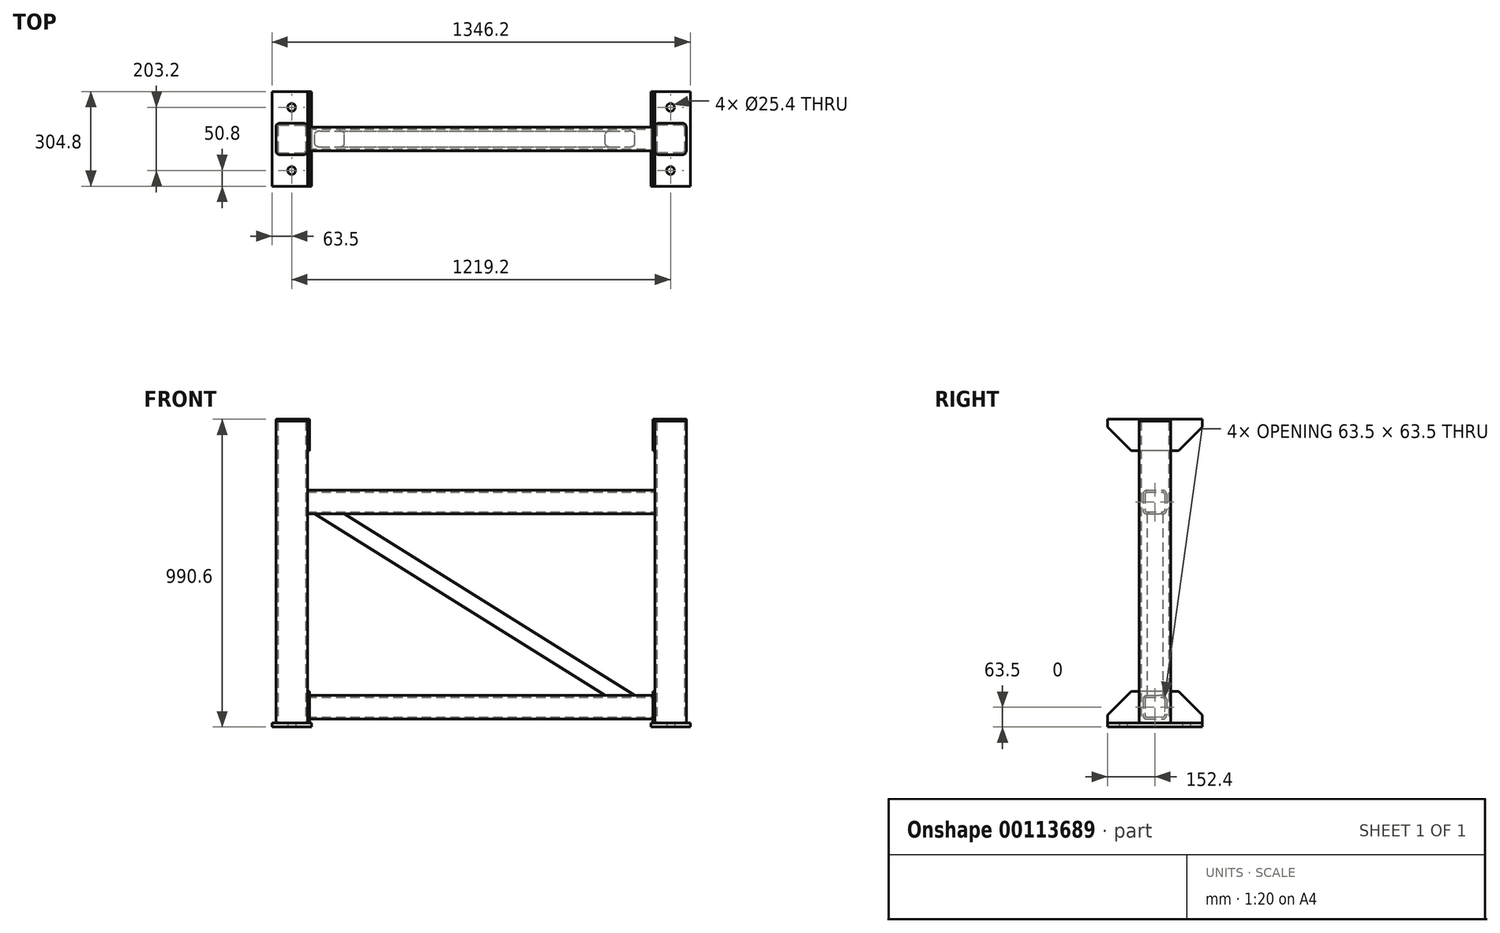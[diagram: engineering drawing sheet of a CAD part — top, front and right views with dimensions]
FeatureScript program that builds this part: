
annotation { "Feature Type Name" : "Feature", "Feature Type Description" : "" }
export const myFeature = defineFeature(function(context is Context, id is Id, definition is map)
    precondition{}
    {
        {
            var Q0;
            Q0=qCreatedBy(makeId("Top.planeOp"),FACE);
            var sketch = newSketch(context, id + "F0", { "sketchPlane" : qUnion([Q0])});
            skLineSegment(sketch, "E0", {"start": v(-609.6, 0) * mm, "end": v(157.5, 0) * mm, "construction": true});
            skLineSegment(sketch, "E1", {"start": v(0, 108.34) * mm, "end": v(0, -86.64) * mm, "construction": true});
            skLineSegment(sketch, "E2.0", {"start": v(-609.6, 108.34) * mm, "end": v(-609.6, -86.64) * mm, "construction": true});
            skPoint(sketch, "E3.orphan", {"position": v(-161.92, 0) * mm});
            skLineSegment(sketch, "E4.bottom", {"start": v(-673.1, 152.4) * mm, "end": v(-546.1, 152.4) * mm});
            skLineSegment(sketch, "E4.top", {"start": v(-673.1, -152.4) * mm, "end": v(-546.1, -152.4) * mm});
            skLineSegment(sketch, "E4.left", {"start": v(-673.1, 152.4) * mm, "end": v(-673.1, -152.4) * mm});
            skLineSegment(sketch, "E4.right", {"start": v(-546.1, 152.4) * mm, "end": v(-546.1, -152.4) * mm});
            skPoint(sketch, "E4.middle", {"position": v(-609.6, 0) * mm});
            skLineSegment(sketch, "E5.0", {"start": v(-609.6, 101.6) * mm, "end": v(157.5, 101.6) * mm, "construction": true});
            skCircle(sketch, "E6", {"center": v(-609.6, 101.6) * mm, "radius": 12.7 * mm});
            skCircle(sketch, "E7.MirrorC", {"center": v(-609.6, -101.6) * mm, "radius": 12.7 * mm});
            skSolve(sketch);
        }
        {
            var Q0;
            Q0 = qSketchRegion(id + "F0", true);
            extrude(context, id + "F1", {"entities" : qUnion([Q0]), "depth" : 12.7 * mm});
        }
        {
            var Q0;
            Q0=makeQuery(id+"F1.opExtrude","CAP_FACE",FACE,{"disambiguationData":[OSD([sQuery(id+"F0.wireOp",EDGE,"E4.bottom"),sQuery(id+"F0.wireOp",EDGE,"E4.top"),sQuery(id+"F0.wireOp",EDGE,"E4.left"),sQuery(id+"F0.wireOp",EDGE,"E4.right"),sQuery(id+"F0.wireOp",EDGE,"E6"),sQuery(id+"F0.wireOp",EDGE,"E7.MirrorC")])],"isStart":false});
            var sketch = newSketch(context, id + "F2", { "sketchPlane" : qUnion([Q0])});
            skLineSegment(sketch, "E8", {"start": v(-673.1, 0) * mm, "end": v(-546.1, 0) * mm, "construction": true});
            skLineSegment(sketch, "E9.bottom", {"start": v(-647.7, 50.8) * mm, "end": v(-571.5, 50.8) * mm});
            skLineSegment(sketch, "E9.top", {"start": v(-647.7, -50.8) * mm, "end": v(-571.5, -50.8) * mm});
            skLineSegment(sketch, "E9.left", {"start": v(-660.4, 38.1) * mm, "end": v(-660.4, -38.1) * mm});
            skLineSegment(sketch, "E9.right", {"start": v(-558.8, 38.1) * mm, "end": v(-558.8, -38.1) * mm});
            skPoint(sketch, "E9.middle", {"position": v(-609.6, 0) * mm});
            skPoint(sketch, "E10.visualSharp", {"position": v(-660.4, 50.8) * mm});
            skArc(sketch, "E10.filletArc", {"start": v(-647.7, 50.8) * mm, "mid": v(-656.68, 47.08) * mm, "end": v(-660.4, 38.1) * mm});
            skPoint(sketch, "E11.visualSharp", {"position": v(-558.8, 50.8) * mm});
            skArc(sketch, "E11.filletArc", {"start": v(-558.8, 38.1) * mm, "mid": v(-562.52, 47.08) * mm, "end": v(-571.5, 50.8) * mm});
            skPoint(sketch, "E12.visualSharp", {"position": v(-558.8, -50.8) * mm});
            skArc(sketch, "E12.filletArc", {"start": v(-571.5, -50.8) * mm, "mid": v(-562.52, -47.08) * mm, "end": v(-558.8, -38.1) * mm});
            skPoint(sketch, "E13.visualSharp", {"position": v(-660.4, -50.8) * mm});
            skArc(sketch, "E13.filletArc", {"start": v(-660.4, -38.1) * mm, "mid": v(-656.68, -47.08) * mm, "end": v(-647.7, -50.8) * mm});
            skArc(sketch, "E14.0", {"start": v(-647.7, 44.45) * mm, "mid": v(-652.2, 42.6) * mm, "end": v(-654.05, 38.1) * mm});
            skLineSegment(sketch, "E14.1", {"start": v(-654.05, 38.1) * mm, "end": v(-654.05, -38.1) * mm});
            skLineSegment(sketch, "E14.2", {"start": v(-647.7, 44.45) * mm, "end": v(-571.5, 44.45) * mm});
            skArc(sketch, "E14.3", {"start": v(-654.05, -38.1) * mm, "mid": v(-652.2, -42.6) * mm, "end": v(-647.7, -44.45) * mm});
            skArc(sketch, "E14.4", {"start": v(-565.15, 38.1) * mm, "mid": v(-567, 42.6) * mm, "end": v(-571.5, 44.45) * mm});
            skLineSegment(sketch, "E14.5", {"start": v(-565.15, 38.1) * mm, "end": v(-565.15, -38.1) * mm});
            skArc(sketch, "E14.6", {"start": v(-571.5, -44.45) * mm, "mid": v(-567, -42.6) * mm, "end": v(-565.15, -38.1) * mm});
            skLineSegment(sketch, "E14.7", {"start": v(-647.7, -44.45) * mm, "end": v(-571.5, -44.45) * mm});
            skSolve(sketch);
        }
        {
            var Q0;
            Q0 = qSketchRegion(id + "F2", true);
            extrude(context, id + "F3", {"entities" : qUnion([Q0]), "operationType" : NewBodyOperationType.ADD, "depth" : 971.55 * mm});
        }
        {
            var Q0;
            Q0=makeQuery(id+"F3.opExtrude","CAP_FACE",FACE,{"disambiguationData":[OSD([sQuery(id+"F2.wireOp",EDGE,"E9.bottom"),sQuery(id+"F2.wireOp",EDGE,"E9.top"),sQuery(id+"F2.wireOp",EDGE,"E9.left"),sQuery(id+"F2.wireOp",EDGE,"E9.right"),sQuery(id+"F2.wireOp",EDGE,"E10.filletArc"),sQuery(id+"F2.wireOp",EDGE,"E11.filletArc"),sQuery(id+"F2.wireOp",EDGE,"E12.filletArc"),sQuery(id+"F2.wireOp",EDGE,"E13.filletArc"),sQuery(id+"F2.wireOp",EDGE,"E14.0"),sQuery(id+"F2.wireOp",EDGE,"E14.1"),sQuery(id+"F2.wireOp",EDGE,"E14.2"),sQuery(id+"F2.wireOp",EDGE,"E14.3"),sQuery(id+"F2.wireOp",EDGE,"E14.4"),sQuery(id+"F2.wireOp",EDGE,"E14.5"),sQuery(id+"F2.wireOp",EDGE,"E14.6"),sQuery(id+"F2.wireOp",EDGE,"E14.7")])],"isStart":false});
            var sketch = newSketch(context, id + "F4", { "sketchPlane" : qUnion([Q0])});
            skLineSegment(sketch, "E15.0", {"start": v(-660.4, 38.1) * mm, "end": v(-660.4, -38.1) * mm});
            skArc(sketch, "E16.0", {"start": v(-647.7, 50.8) * mm, "mid": v(-656.68, 47.08) * mm, "end": v(-660.4, 38.1) * mm});
            skLineSegment(sketch, "E17.0", {"start": v(-647.7, 50.8) * mm, "end": v(-571.5, 50.8) * mm});
            skArc(sketch, "E18.0", {"start": v(-558.8, 38.1) * mm, "mid": v(-562.52, 47.08) * mm, "end": v(-571.5, 50.8) * mm});
            skLineSegment(sketch, "E19.0", {"start": v(-558.8, 38.1) * mm, "end": v(-558.8, -38.1) * mm});
            skArc(sketch, "E20.0", {"start": v(-571.5, -50.8) * mm, "mid": v(-562.52, -47.08) * mm, "end": v(-558.8, -38.1) * mm});
            skLineSegment(sketch, "E21.0", {"start": v(-647.7, -50.8) * mm, "end": v(-571.5, -50.8) * mm});
            skArc(sketch, "E22.0", {"start": v(-660.4, -38.1) * mm, "mid": v(-656.68, -47.08) * mm, "end": v(-647.7, -50.8) * mm});
            skSolve(sketch);
        }
        {
            var Q0;
            Q0 = qSketchRegion(id + "F4", true);
            extrude(context, id + "F5", {"entities" : qUnion([Q0]), "depth" : 6.35 * mm});
        }
        {
            var Q0;
            Q0=makeQuery(id+"F5.boolean.opBoolean","MERGE",FACE,{"derivedFrom":[makeQuery(id+"F3.opExtrude","SWEPT_FACE",FACE,{"disambiguationData":[OSD([sQuery(id+"F2.wireOp",EDGE,"E9.right")])]}),makeQuery(id+"F5.opExtrude","SWEPT_FACE",FACE,{"disambiguationData":[OSD([sQuery(id+"F4.wireOp",EDGE,"E19.0")])]})]});
            var sketch = newSketch(context, id + "F6", { "sketchPlane" : qUnion([Q0])});
            skLineSegment(sketch, "E23.0", {"start": v(152.4, 12.7) * mm, "end": v(-152.4, 12.7) * mm});
            skLineSegment(sketch, "E24.0", {"start": v(76.2, 114.3) * mm, "end": v(-76.2, 114.3) * mm});
            skLineSegment(sketch, "E25", {"start": v(-152.4, 38.1) * mm, "end": v(-152.4, 12.7) * mm});
            skLineSegment(sketch, "E26", {"start": v(152.4, 38.1) * mm, "end": v(152.4, 12.7) * mm});
            skLineSegment(sketch, "E27", {"start": v(-152.4, 38.1) * mm, "end": v(-76.2, 114.3) * mm});
            skLineSegment(sketch, "E28", {"start": v(76.2, 114.3) * mm, "end": v(152.4, 38.1) * mm});
            skSolve(sketch);
        }
        {
            var Q0;
            Q0 = qSketchRegion(id + "F6", true);
            extrude(context, id + "F7", {"entities" : qUnion([Q0]), "depth" : 6.35 * mm});
        }
        {
            var Q0;
            Q0=makeQuery(id+"F7.opExtrude","SWEPT_BODY",BODY,{"disambiguationData":[OSD([sQuery(id+"F6.wireOp",EDGE,"E23.0"),sQuery(id+"F6.wireOp",EDGE,"E24.0"),sQuery(id+"F6.wireOp",EDGE,"E25"),sQuery(id+"F6.wireOp",EDGE,"E26"),sQuery(id+"F6.wireOp",EDGE,"E27"),sQuery(id+"F6.wireOp",EDGE,"E28")])]});
            var Q1;
            Q1=makeQuery(id+"F5.opExtrude","CAP_FACE",FACE,{"disambiguationData":[OSD([sQuery(id+"F4.wireOp",EDGE,"E15.0"),sQuery(id+"F4.wireOp",EDGE,"E16.0"),sQuery(id+"F4.wireOp",EDGE,"E17.0"),sQuery(id+"F4.wireOp",EDGE,"E18.0"),sQuery(id+"F4.wireOp",EDGE,"E19.0"),sQuery(id+"F4.wireOp",EDGE,"E20.0"),sQuery(id+"F4.wireOp",EDGE,"E21.0"),sQuery(id+"F4.wireOp",EDGE,"E22.0")])],"isStart":false});
            mirror(context, id + "F8", {"entities" : qUnion([Q0]), "mirrorPlane" : qUnion([Q1])});
        }
        {
            var Q0;
            Q0=makeQuery(id+"F8.opPattern","COPY",BODY,{"derivedFrom":makeQuery(id+"F7.opExtrude","SWEPT_BODY",BODY,{"disambiguationData":[OSD([sQuery(id+"F6.wireOp",EDGE,"E23.0"),sQuery(id+"F6.wireOp",EDGE,"E24.0"),sQuery(id+"F6.wireOp",EDGE,"E25"),sQuery(id+"F6.wireOp",EDGE,"E26"),sQuery(id+"F6.wireOp",EDGE,"E27"),sQuery(id+"F6.wireOp",EDGE,"E28")])]}),"instanceName":"1"});
            var Q1;
            Q1=makeQuery(id+"F3.opExtrude","SWEPT_EDGE",EDGE,{"disambiguationData":[OSD([sQuery(id+"F2.wireOp",EDGE,"E9.bottom"),sQuery(id+"F2.wireOp",EDGE,"E11.filletArc")])]});
            transform(context, id + "F9", {"entities" : qUnion([Q0]), "transformType" : TransformType.TRANSLATION_ENTITY, "oppositeDirectionEntity" : false, "transformLine" : qUnion([Q1]), "makeCopy" : false});
        }
        {
            var Q0;
            Q0=makeQuery(id+"F8.opPattern","COPY",BODY,{"derivedFrom":makeQuery(id+"F7.opExtrude","SWEPT_BODY",BODY,{"disambiguationData":[OSD([sQuery(id+"F6.wireOp",EDGE,"E23.0"),sQuery(id+"F6.wireOp",EDGE,"E24.0"),sQuery(id+"F6.wireOp",EDGE,"E25"),sQuery(id+"F6.wireOp",EDGE,"E26"),sQuery(id+"F6.wireOp",EDGE,"E27"),sQuery(id+"F6.wireOp",EDGE,"E28")])]}),"instanceName":"1"});
            var Q1;
            Q1=makeQuery(id+"F8.opPattern","COPY",EDGE,{"derivedFrom":makeQuery(id+"F7.opExtrude","CAP_EDGE",EDGE,{"disambiguationData":[OSD([sQuery(id+"F6.wireOp",EDGE,"E26")])],"isStart":false}),"instanceName":"1"});
            transform(context, id + "F10", {"entities" : qUnion([Q0]), "transformType" : TransformType.TRANSLATION_DISTANCE, "transformDirection" : qUnion([Q1]), "distance" : 6.35 * mm, "oppositeDirection" : true, "makeCopy" : false});
        }
        {
            var Q0;
            Q0=makeQuery(id+"F3.opExtrude","SWEPT_FACE",FACE,{"disambiguationData":[OSD([sQuery(id+"F2.wireOp",EDGE,"E9.right")])]});
            var sketch = newSketch(context, id + "F11", { "sketchPlane" : qUnion([Q0])});
            skLineSegment(sketch, "E29.0", {"start": v(152.4, 0) * mm, "end": v(-152.4, 0) * mm, "construction": true});
            skLineSegment(sketch, "E30.0", {"start": v(152.4, 63.5) * mm, "end": v(-152.4, 63.5) * mm, "construction": true});
            skLineSegment(sketch, "E31.bottom", {"start": v(-25.4, 101.6) * mm, "end": v(25.4, 101.6) * mm});
            skLineSegment(sketch, "E31.top", {"start": v(-25.4, 25.4) * mm, "end": v(25.4, 25.4) * mm});
            skLineSegment(sketch, "E31.left", {"start": v(-38.1, 88.9) * mm, "end": v(-38.1, 38.1) * mm});
            skLineSegment(sketch, "E31.right", {"start": v(38.1, 88.9) * mm, "end": v(38.1, 38.1) * mm});
            skPoint(sketch, "E31.middle", {"position": v(0, 63.5) * mm});
            skPoint(sketch, "E32.visualSharp", {"position": v(-38.1, 101.6) * mm});
            skArc(sketch, "E32.filletArc", {"start": v(-25.4, 101.6) * mm, "mid": v(-34.38, 97.88) * mm, "end": v(-38.1, 88.9) * mm});
            skPoint(sketch, "E33.visualSharp", {"position": v(38.1, 101.6) * mm});
            skArc(sketch, "E33.filletArc", {"start": v(38.1, 88.9) * mm, "mid": v(34.38, 97.88) * mm, "end": v(25.4, 101.6) * mm});
            skPoint(sketch, "E34.visualSharp", {"position": v(38.1, 25.4) * mm});
            skArc(sketch, "E34.filletArc", {"start": v(25.4, 25.4) * mm, "mid": v(34.38, 29.12) * mm, "end": v(38.1, 38.1) * mm});
            skPoint(sketch, "E35.visualSharp", {"position": v(-38.1, 25.4) * mm});
            skArc(sketch, "E35.filletArc", {"start": v(-38.1, 38.1) * mm, "mid": v(-34.38, 29.12) * mm, "end": v(-25.4, 25.4) * mm});
            skArc(sketch, "E36.0", {"start": v(-25.4, 95.25) * mm, "mid": v(-29.9, 93.4) * mm, "end": v(-31.75, 88.9) * mm});
            skLineSegment(sketch, "E36.1", {"start": v(-31.75, 88.9) * mm, "end": v(-31.75, 38.1) * mm});
            skLineSegment(sketch, "E36.2", {"start": v(-25.4, 95.25) * mm, "end": v(25.4, 95.25) * mm});
            skArc(sketch, "E36.3", {"start": v(-31.75, 38.1) * mm, "mid": v(-29.9, 33.6) * mm, "end": v(-25.4, 31.75) * mm});
            skArc(sketch, "E36.4", {"start": v(31.75, 88.9) * mm, "mid": v(29.9, 93.4) * mm, "end": v(25.4, 95.25) * mm});
            skLineSegment(sketch, "E36.5", {"start": v(31.75, 88.9) * mm, "end": v(31.75, 38.1) * mm});
            skArc(sketch, "E36.6", {"start": v(25.4, 31.75) * mm, "mid": v(29.9, 33.6) * mm, "end": v(31.75, 38.1) * mm});
            skLineSegment(sketch, "E36.7", {"start": v(-25.4, 31.75) * mm, "end": v(25.4, 31.75) * mm});
            skPoint(sketch, "E37.0.1.0", {"position": v(38.1, 762) * mm});
            skPoint(sketch, "E37.0.1.1", {"position": v(38.1, 685.8) * mm});
            skPoint(sketch, "E37.0.1.2", {"position": v(-38.1, 762) * mm});
            skPoint(sketch, "E37.0.1.3", {"position": v(-38.1, 685.8) * mm});
            skLineSegment(sketch, "E37.0.1.4", {"start": v(31.75, 749.3) * mm, "end": v(31.75, 698.5) * mm});
            skPoint(sketch, "E37.0.1.5", {"position": v(0, 723.9) * mm});
            skLineSegment(sketch, "E37.0.1.6", {"start": v(-38.1, 749.3) * mm, "end": v(-38.1, 698.5) * mm});
            skLineSegment(sketch, "E37.0.1.7", {"start": v(38.1, 749.3) * mm, "end": v(38.1, 698.5) * mm});
            skLineSegment(sketch, "E37.0.1.8", {"start": v(-31.75, 749.3) * mm, "end": v(-31.75, 698.5) * mm});
            skLineSegment(sketch, "E37.0.1.9", {"start": v(-25.4, 685.8) * mm, "end": v(25.4, 685.8) * mm});
            skLineSegment(sketch, "E37.0.1.10", {"start": v(-25.4, 762) * mm, "end": v(25.4, 762) * mm});
            skLineSegment(sketch, "E37.0.1.11", {"start": v(-25.4, 692.15) * mm, "end": v(25.4, 692.15) * mm});
            skLineSegment(sketch, "E37.0.1.12", {"start": v(-25.4, 755.65) * mm, "end": v(25.4, 755.65) * mm});
            skArc(sketch, "E37.0.1.13", {"start": v(25.4, 692.15) * mm, "mid": v(29.9, 694) * mm, "end": v(31.75, 698.5) * mm});
            skArc(sketch, "E37.0.1.14", {"start": v(-25.4, 762) * mm, "mid": v(-34.38, 758.28) * mm, "end": v(-38.1, 749.3) * mm});
            skArc(sketch, "E37.0.1.15", {"start": v(38.1, 749.3) * mm, "mid": v(34.38, 758.28) * mm, "end": v(25.4, 762) * mm});
            skArc(sketch, "E37.0.1.16", {"start": v(25.4, 685.8) * mm, "mid": v(34.38, 689.52) * mm, "end": v(38.1, 698.5) * mm});
            skArc(sketch, "E37.0.1.17", {"start": v(-25.4, 755.65) * mm, "mid": v(-29.9, 753.8) * mm, "end": v(-31.75, 749.3) * mm});
            skArc(sketch, "E37.0.1.18", {"start": v(-31.75, 698.5) * mm, "mid": v(-29.9, 694) * mm, "end": v(-25.4, 692.15) * mm});
            skArc(sketch, "E37.0.1.19", {"start": v(31.75, 749.3) * mm, "mid": v(29.9, 753.8) * mm, "end": v(25.4, 755.65) * mm});
            skArc(sketch, "E37.0.1.20", {"start": v(-38.1, 698.5) * mm, "mid": v(-34.38, 689.52) * mm, "end": v(-25.4, 685.8) * mm});
            skLineSegment(sketch, "E37.direction1", {"start": v(-38.1, 25.4) * mm, "end": v(-12.7, 25.4) * mm, "construction": true});
            skLineSegment(sketch, "E37.direction2", {"start": v(-38.1, 25.4) * mm, "end": v(-38.1, 685.8) * mm, "construction": true});
            skSolve(sketch);
        }
        {
            var Q0;
            Q0 = qSketchRegion(id + "F11", true);
            extrude(context, id + "F12", {"entities" : qUnion([Q0]), "depth" : 1117.6 * mm});
        }
        {
            var Q0;
            Q0=makeQuery(id+"F1.opExtrude","SWEPT_BODY",BODY,{"disambiguationData":[OSD([sQuery(id+"F0.wireOp",EDGE,"E4.bottom"),sQuery(id+"F0.wireOp",EDGE,"E4.top"),sQuery(id+"F0.wireOp",EDGE,"E4.left"),sQuery(id+"F0.wireOp",EDGE,"E4.right"),sQuery(id+"F0.wireOp",EDGE,"E6"),sQuery(id+"F0.wireOp",EDGE,"E7.MirrorC")])]});
            var Q1;
            Q1=makeQuery(id+"F7.opExtrude","SWEPT_BODY",BODY,{"disambiguationData":[OSD([sQuery(id+"F6.wireOp",EDGE,"E23.0"),sQuery(id+"F6.wireOp",EDGE,"E24.0"),sQuery(id+"F6.wireOp",EDGE,"E25"),sQuery(id+"F6.wireOp",EDGE,"E26"),sQuery(id+"F6.wireOp",EDGE,"E27"),sQuery(id+"F6.wireOp",EDGE,"E28")])]});
            var Q2;
            Q2=makeQuery(id+"F5.opExtrude","SWEPT_BODY",BODY,{"disambiguationData":[OSD([sQuery(id+"F4.wireOp",EDGE,"E15.0"),sQuery(id+"F4.wireOp",EDGE,"E16.0"),sQuery(id+"F4.wireOp",EDGE,"E17.0"),sQuery(id+"F4.wireOp",EDGE,"E18.0"),sQuery(id+"F4.wireOp",EDGE,"E19.0"),sQuery(id+"F4.wireOp",EDGE,"E20.0"),sQuery(id+"F4.wireOp",EDGE,"E21.0"),sQuery(id+"F4.wireOp",EDGE,"E22.0")])]});
            var Q3;
            Q3=makeQuery(id+"F8.opPattern","COPY",BODY,{"derivedFrom":makeQuery(id+"F7.opExtrude","SWEPT_BODY",BODY,{"disambiguationData":[OSD([sQuery(id+"F6.wireOp",EDGE,"E23.0"),sQuery(id+"F6.wireOp",EDGE,"E24.0"),sQuery(id+"F6.wireOp",EDGE,"E25"),sQuery(id+"F6.wireOp",EDGE,"E26"),sQuery(id+"F6.wireOp",EDGE,"E27"),sQuery(id+"F6.wireOp",EDGE,"E28")])]}),"instanceName":"1"});
            var Q4;
            Q4=makeQuery(id+"F12.opExtrude","SWEPT_BODY",BODY,{"disambiguationData":[OSD([sQuery(id+"F11.wireOp",EDGE,"E31.bottom"),sQuery(id+"F11.wireOp",EDGE,"E31.top"),sQuery(id+"F11.wireOp",EDGE,"E31.left"),sQuery(id+"F11.wireOp",EDGE,"E31.right"),sQuery(id+"F11.wireOp",EDGE,"E32.filletArc"),sQuery(id+"F11.wireOp",EDGE,"E33.filletArc"),sQuery(id+"F11.wireOp",EDGE,"E34.filletArc"),sQuery(id+"F11.wireOp",EDGE,"E35.filletArc"),sQuery(id+"F11.wireOp",EDGE,"E36.0"),sQuery(id+"F11.wireOp",EDGE,"E36.1"),sQuery(id+"F11.wireOp",EDGE,"E36.2"),sQuery(id+"F11.wireOp",EDGE,"E36.3"),sQuery(id+"F11.wireOp",EDGE,"E36.4"),sQuery(id+"F11.wireOp",EDGE,"E36.5"),sQuery(id+"F11.wireOp",EDGE,"E36.6"),sQuery(id+"F11.wireOp",EDGE,"E36.7")])]});
            var Q5;
            Q5=makeQuery(id+"F12.opExtrude","SWEPT_BODY",BODY,{"disambiguationData":[OSD([sQuery(id+"F11.wireOp",EDGE,"E37.0.1.4"),sQuery(id+"F11.wireOp",EDGE,"E37.0.1.6"),sQuery(id+"F11.wireOp",EDGE,"E37.0.1.7"),sQuery(id+"F11.wireOp",EDGE,"E37.0.1.8"),sQuery(id+"F11.wireOp",EDGE,"E37.0.1.9"),sQuery(id+"F11.wireOp",EDGE,"E37.0.1.10"),sQuery(id+"F11.wireOp",EDGE,"E37.0.1.11"),sQuery(id+"F11.wireOp",EDGE,"E37.0.1.12"),sQuery(id+"F11.wireOp",EDGE,"E37.0.1.13"),sQuery(id+"F11.wireOp",EDGE,"E37.0.1.14"),sQuery(id+"F11.wireOp",EDGE,"E37.0.1.15"),sQuery(id+"F11.wireOp",EDGE,"E37.0.1.16"),sQuery(id+"F11.wireOp",EDGE,"E37.0.1.17"),sQuery(id+"F11.wireOp",EDGE,"E37.0.1.18"),sQuery(id+"F11.wireOp",EDGE,"E37.0.1.19"),sQuery(id+"F11.wireOp",EDGE,"E37.0.1.20")])]});
            var Q6;
            Q6=qCreatedBy(makeId("Right.planeOp"),FACE);
            mirror(context, id + "F13", {"entities" : qUnion([Q0, Q1, Q2, Q3, Q4, Q5]), "mirrorPlane" : qUnion([Q6])});
        }
        {
            var Q0;
            Q0=qCreatedBy(makeId("Front.planeOp"),FACE);
            var sketch = newSketch(context, id + "F14", { "sketchPlane" : qUnion([Q0])});
            skLineSegment(sketch, "E38.0", {"start": v(673.1, 0) * mm, "end": v(546.1, 0) * mm, "construction": true});
            skLineSegment(sketch, "E39.0", {"start": v(-673.1, 0) * mm, "end": v(-546.1, 0) * mm, "construction": true});
            skLineSegment(sketch, "E40.0", {"start": v(558.8, 762) * mm, "end": v(-609.6, 762) * mm, "construction": true});
            skLineSegment(sketch, "E41", {"start": v(-609.6, 0) * mm, "end": v(-609.6, 762) * mm, "construction": true});
            skLineSegment(sketch, "E42", {"start": v(609.6, 0) * mm, "end": v(609.6, 857.9) * mm, "construction": true});
            skPoint(sketch, "E42.endSnap0", {"position": v(609.6, 0) * mm});
            skPoint(sketch, "E43.orphan", {"position": v(-558.8, 762) * mm});
            skLineSegment(sketch, "E44", {"start": v(-609.6, 762) * mm, "end": v(609.6, 0) * mm, "construction": true});
            skLineSegment(sketch, "E45.0", {"start": v(558.8, 685.8) * mm, "end": v(-558.8, 685.8) * mm, "construction": true});
            skLineSegment(sketch, "E46.0", {"start": v(558.8, 101.6) * mm, "end": v(-558.8, 101.6) * mm, "construction": true});
            skLineSegment(sketch, "E47.0", {"start": v(-623.06, 740.46) * mm, "end": v(-609.6, 732.05) * mm, "construction": true});
            skLineSegment(sketch, "E48.MirrorCS", {"start": v(-596.14, 783.54) * mm, "end": v(-561.68, 762) * mm, "construction": true});
            skLineSegment(sketch, "E49.trimOffspring", {"start": v(-439.76, 685.8) * mm, "end": v(494.96, 101.6) * mm});
            skLineSegment(sketch, "E50.trimOffspring", {"start": v(-535.6, 685.8) * mm, "end": v(399.12, 101.6) * mm});
            skLineSegment(sketch, "E51.trimOffspring", {"start": v(561.68, 0) * mm, "end": v(596.14, -21.54) * mm, "construction": true});
            skLineSegment(sketch, "E52.trimOffspring", {"start": v(609.6, 29.95) * mm, "end": v(623.06, 21.54) * mm, "construction": true});
            skLineSegment(sketch, "E53", {"start": v(-535.6, 685.8) * mm, "end": v(-439.76, 685.8) * mm});
            skLineSegment(sketch, "E54", {"start": v(399.12, 101.6) * mm, "end": v(494.96, 101.6) * mm});
            skSolve(sketch);
        }
        {
            var Q0;
            Q0 = qSketchRegion(id + "F14", true);
            extrude(context, id + "F15", {"entities" : qUnion([Q0]), "endBound" : BoundingType.SYMMETRIC, "depth" : 50.8 * mm});
        }
        {
            var Q0;
            Q0=makeQuery(id+"F15.opExtrude","CAP_EDGE",EDGE,{"disambiguationData":[OSD([sQuery(id+"F14.wireOp",EDGE,"E49.trimOffspring")])],"isStart":false});
            var Q1;
            Q1=makeQuery(id+"F15.opExtrude","CAP_EDGE",EDGE,{"disambiguationData":[OSD([sQuery(id+"F14.wireOp",EDGE,"E50.trimOffspring")])],"isStart":false});
            var Q2;
            Q2=makeQuery(id+"F15.opExtrude","CAP_EDGE",EDGE,{"disambiguationData":[OSD([sQuery(id+"F14.wireOp",EDGE,"E49.trimOffspring")])],"isStart":true});
            var Q3;
            Q3=makeQuery(id+"F15.opExtrude","CAP_EDGE",EDGE,{"disambiguationData":[OSD([sQuery(id+"F14.wireOp",EDGE,"E50.trimOffspring")])],"isStart":true});
            fillet(context, id + "F16", {"entities" : qUnion([Q0, Q1, Q2, Q3]), "radius" : 9.65 * mm, "tangentPropagation" : true, "allowEdgeOverflow" : false});
        }
    });
